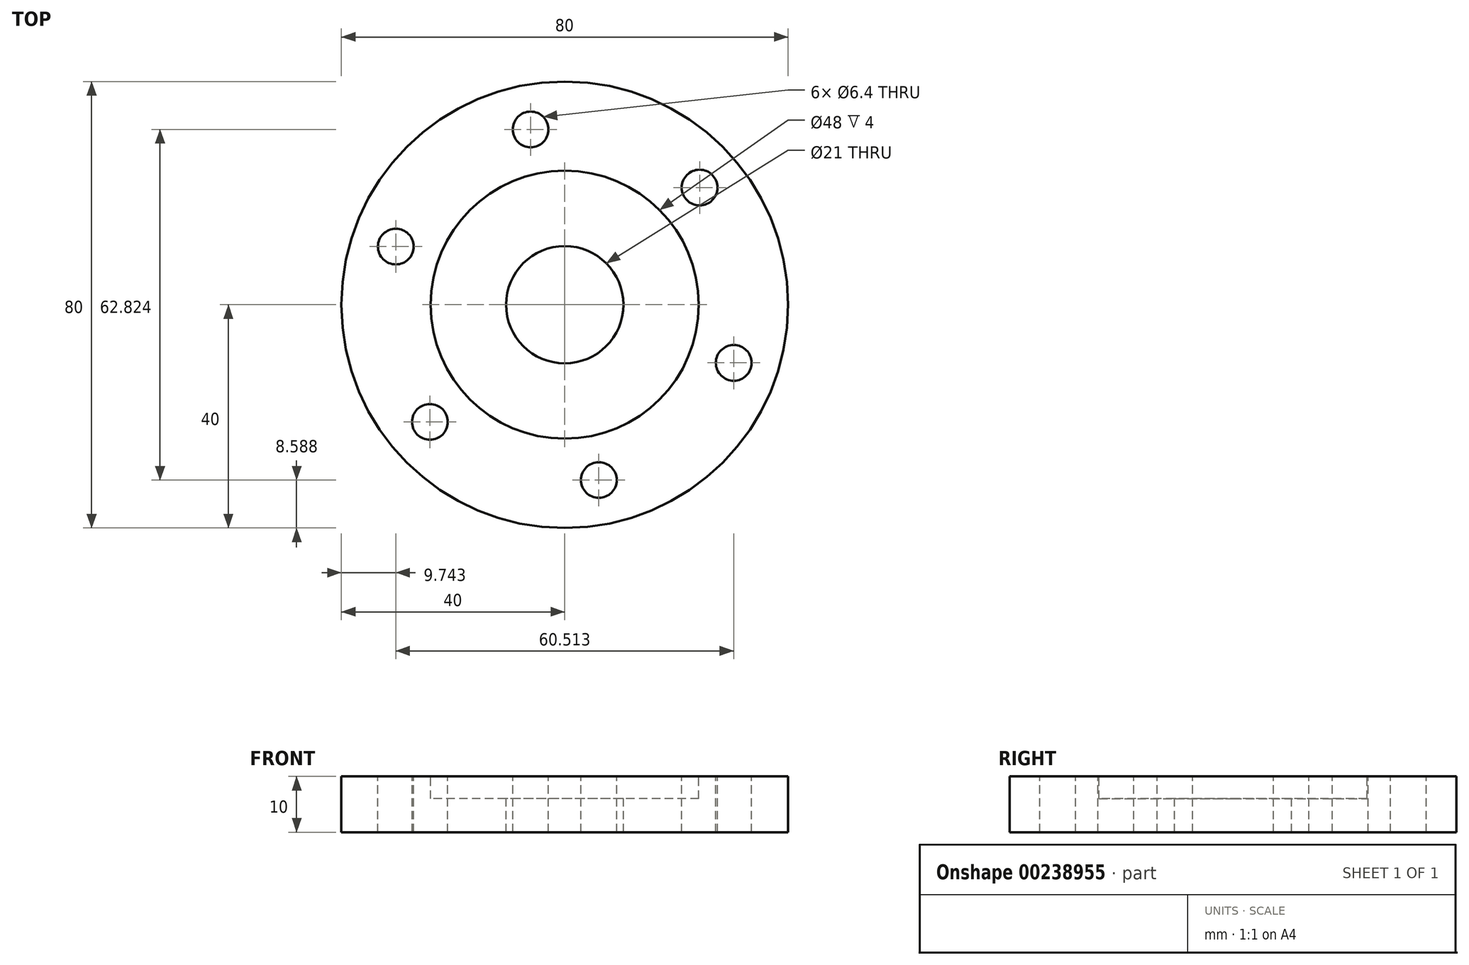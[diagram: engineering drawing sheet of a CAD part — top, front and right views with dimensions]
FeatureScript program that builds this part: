
annotation { "Feature Type Name" : "Feature", "Feature Type Description" : "" }
export const myFeature = defineFeature(function(context is Context, id is Id, definition is map)
    precondition{}
    {
        {
            var Q0;
            Q0=qCreatedBy(makeId("Top.planeOp"),FACE);
            var sketch = newSketch(context, id + "F0", { "sketchPlane" : qUnion([Q0])});
            skCircle(sketch, "E0", {"center": v(0, 0) * mm, "radius": 40 * mm});
            skLineSegment(sketch, "E1", {"start": v(0, 0) * mm, "end": v(-9.46, 48.68) * mm, "construction": true});
            skCircle(sketch, "E2", {"center": v(0, 0) * mm, "radius": 32 * mm, "construction": true});
            skPoint(sketch, "E3", {"position": v(-6.1, 31.41) * mm});
            skPoint(sketch, "E4.1.0", {"position": v(-30.26, 10.42) * mm});
            skPoint(sketch, "E4.2.0", {"position": v(-24.15, -21) * mm});
            skPoint(sketch, "E4.3.0", {"position": v(6.1, -31.41) * mm});
            skPoint(sketch, "E4.4.0", {"position": v(30.26, -10.42) * mm});
            skPoint(sketch, "E4.5.0", {"position": v(24.15, 21) * mm});
            skSolve(sketch);
        }
        {
            var Q0;
            Q0 = qSketchRegion(id + "F0", true);
            extrude(context, id + "F1", {"entities" : qUnion([Q0]), "oppositeDirection" : true, "depth" : 10 * mm});
        }
        {
            var Q0;
            Q0=qCreatedBy(makeId("Top.planeOp"),FACE);
            var sketch = newSketch(context, id + "F2", { "sketchPlane" : qUnion([Q0])});
            skCircle(sketch, "E5", {"center": v(0, 0) * mm, "radius": 24 * mm});
            skSolve(sketch);
        }
        {
            var Q0;
            Q0 = qSketchRegion(id + "F2", true);
            extrude(context, id + "F3", {"entities" : qUnion([Q0]), "operationType" : NewBodyOperationType.REMOVE, "oppositeDirection" : true, "depth" : 4 * mm, "hasSecondDirection" : true, "secondDirectionOppositeDirection" : false, "secondDirectionDepth" : 10 * mm});
        }
        {
            var Q0;
            Q0=makeQuery(id+"F3.boolean.opBoolean","COPY",FACE,{"derivedFrom":makeQuery(id+"F3.opExtrude","CAP_FACE",FACE,{"disambiguationData":[OSD([sQuery(id+"F2.wireOp",EDGE,"E5")])],"isStart":false})});
            cPlane(context, id + "F4", {"entities" : qUnion([Q0]), "cplaneType" : CPlaneType.OFFSET, "offset" : 0 * mm, "width" : 150 * mm, "height" : 150 * mm});
        }
        {
            var Q0;
            Q0=qCreatedBy(id+"F4.planeOp",FACE);
            var sketch = newSketch(context, id + "F5", { "sketchPlane" : qUnion([Q0])});
            skPoint(sketch, "E6", {"position": v(0, 0) * mm});
            skSolve(sketch);
        }
        {
            var Q0;
            Q0=sQuery(id+"F5.wireOp",VERTEX,"E6");
            var Q1;
            Q1=makeQuery(id+"F1.opExtrude","SWEPT_BODY",BODY,{"disambiguationData":[OSD([sQuery(id+"F0.wireOp",EDGE,"E0")])]});
            hole(context, id + "F6", {"style" : HoleStyle.SIMPLE, "endStyle" : HoleEndStyle.THROUGH, "holeDiameter" : 21 * mm, "locations" : qUnion([Q0]), "scope" : qUnion([Q1]), "isTappedThrough" : true});
        }
        {
            var Q0;
            Q0=sQuery(id+"F0.wireOp",VERTEX,"E3");
            var Q1;
            Q1=sQuery(id+"F0.wireOp",VERTEX,"E4.5.0");
            var Q2;
            Q2=sQuery(id+"F0.wireOp",VERTEX,"E4.4.0");
            var Q3;
            Q3=sQuery(id+"F0.wireOp",VERTEX,"E4.3.0");
            var Q4;
            Q4=sQuery(id+"F0.wireOp",VERTEX,"E4.2.0");
            var Q5;
            Q5=sQuery(id+"F0.wireOp",VERTEX,"E4.1.0");
            var Q6;
            Q6=makeQuery(id+"F1.opExtrude","SWEPT_BODY",BODY,{"disambiguationData":[OSD([sQuery(id+"F0.wireOp",EDGE,"E0")])]});
            hole(context, id + "F7", {"style" : HoleStyle.SIMPLE, "endStyle" : HoleEndStyle.THROUGH, "holeDiameter" : 6.4 * mm, "locations" : qUnion([Q0, Q1, Q2, Q3, Q4, Q5]), "scope" : qUnion([Q6]), "isTappedThrough" : true});
        }
    });
